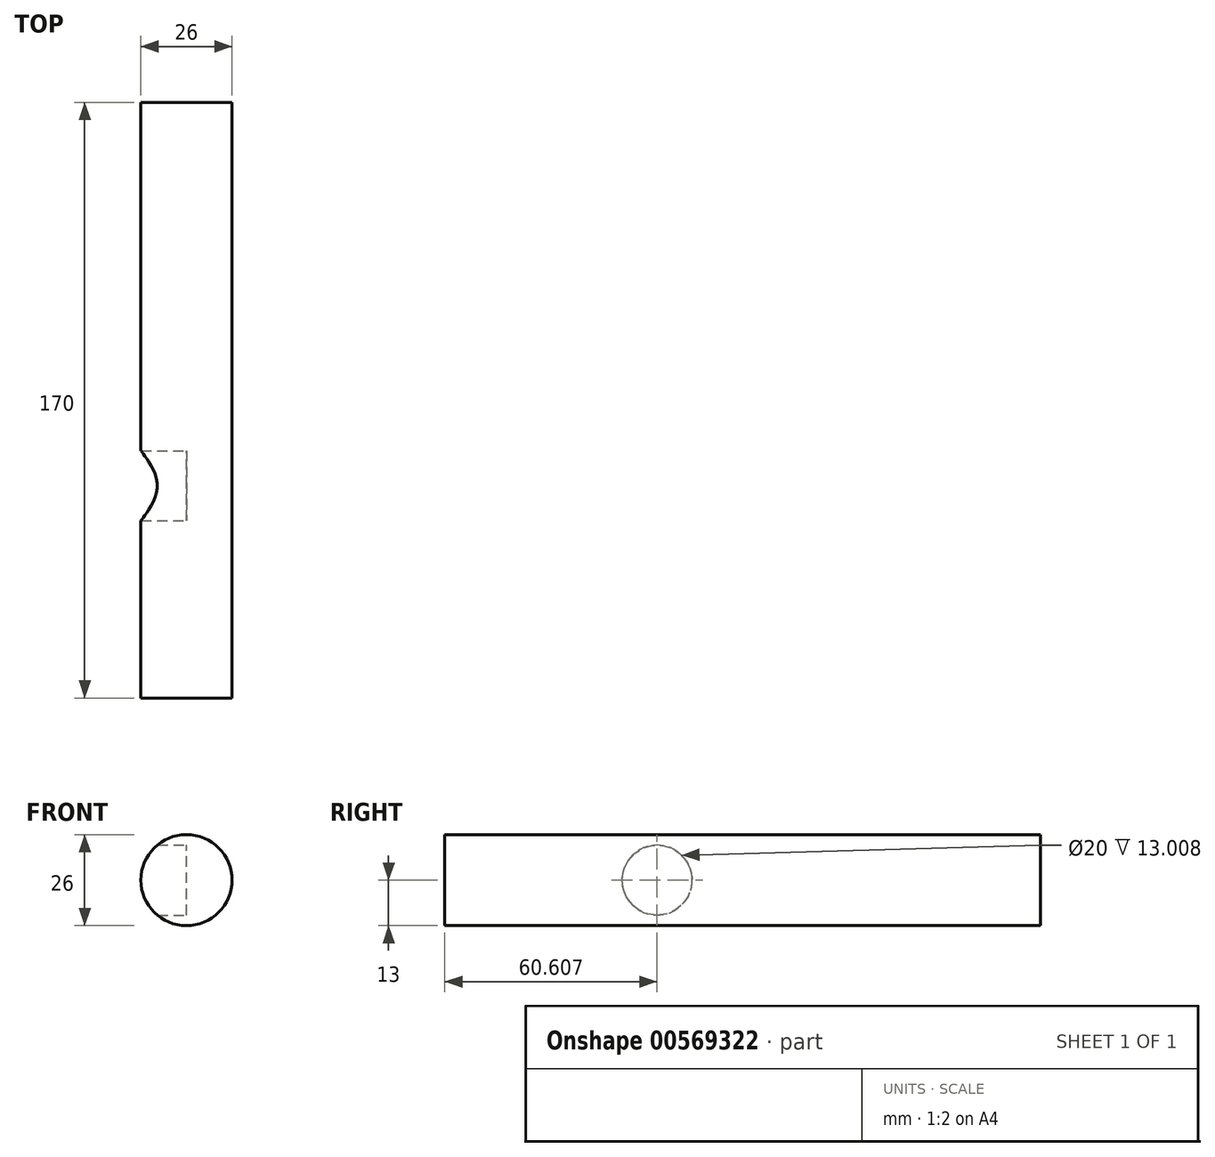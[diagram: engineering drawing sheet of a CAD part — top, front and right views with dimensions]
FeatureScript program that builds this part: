
annotation { "Feature Type Name" : "Feature", "Feature Type Description" : "" }
export const myFeature = defineFeature(function(context is Context, id is Id, definition is map)
    precondition{}
    {
        {
            var Q0;
            Q0=qCreatedBy(makeId("Front.planeOp"),FACE);
            var sketch = newSketch(context, id + "F0", { "sketchPlane" : qUnion([Q0])});
            skCircle(sketch, "E0", {"center": v(0, 0) * mm, "radius": 13 * mm});
            skSolve(sketch);
        }
        {
            var Q0;
            Q0=makeQuery(id+"F0.imprint","IMPRINT",FACE,{"disambiguationData":[TD([[makeQuery(id+"F0.imprint","IMPRINT",EDGE,{"derivedFrom":sQuery(id+"F0.wireOp",EDGE,"E0")}),1.0]])]});
            var Q1;
            Q1=sQuery(id+"F0.wireOp",EDGE,"E0");
            extrude(context, id + "F1", {"entities" : qUnion([Q0]), "surfaceEntities" : qUnion([Q1]), "depth" : 170 * mm, "offsetDistance" : 25 * mm});
        }
        {
            var Q0;
            Q0=qCreatedBy(makeId("Right.planeOp"),FACE);
            var sketch = newSketch(context, id + "F2", { "sketchPlane" : qUnion([Q0])});
            skCircle(sketch, "E1", {"center": v(-109.4, 0) * mm, "radius": 10 * mm});
            skSolve(sketch);
        }
        {
            var Q0;
            Q0=sQuery(id+"F2.wireOp",VERTEX,"E1.center");
            var Q1;
            Q1=makeQuery(id+"F1.opExtrude","SWEPT_BODY",BODY,{"disambiguationData":[OSD([sQuery(id+"F0.wireOp",EDGE,"E0")])]});
            hole(context, id + "F3", {"style" : HoleStyle.SIMPLE, "endStyle" : HoleEndStyle.BLIND, "holeDiameter" : 20 * mm, "majorDiameter" : 5 * mm, "holeDepth" : 25 * mm, "isTappedThrough" : true, "tappedDepth" : 12 * mm, "tapClearance" : 3, "startFromSketch" : true, "locations" : qUnion([Q0]), "scope" : qUnion([Q1])});
        }
    });
